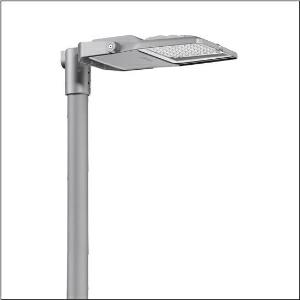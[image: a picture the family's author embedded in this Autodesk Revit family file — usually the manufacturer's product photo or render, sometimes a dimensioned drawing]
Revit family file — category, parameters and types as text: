
# Revit family: floodlight_fl_21_iq_mini___pl33t_5xa7772c4f3a_1e48
name_source: partatom
category: Lighting Fixtures
units: mm (PartAtom-declared; Revit-internal decimal feet)

## family parameters
Cut with Voids When Loaded = No
Host = Face
Light Source = No
Part Type = Normal
Room Calculation Point = No
Round Connector Dimension = Use Diameter
Shared = No

## types (1)
- --- (1 x LED, 12570 lm, 87.2 W, 4000K)
    Apparent Load = 87 VA
    CIE Flux Codes = 26 75 99 100 100
    Color Rendering = 70
    Color Temperature = 4000K
    Default Elevation = 1800 mm
    Description = Floodlight FL 21 iQ mini, floodlight, primary light control with lens, of PMMA, primary optical cover: protective disc, of toughened safety glass, transparent, light distribution: PL33T, light emission: direct distribution, installation type: surface-mounted, LED, High Power LED, rated luminous flux: 12.570lm, luminous efficacy: 144lm/W, light colour: 740, colour temperature: 4000K, control: Auto-Match, Temp-Guard, Night-Set, Smart-Wire, Desk-Remote (wireless, voltage-free reading and setting of iQ features in the workshop via application-optimized NFC function/RFID function), optimised constant luminous flux control (CLO 2.0), Light-Fading, Lumen-Switch, with terminal, 6-pole, mains connection: 220..240V, AC, 50/60Hz, start of lifetime: 87W, end of service life: 92W, reduction: 40W, luminaire housing, of diecast aluminium, powder-coated, Siteco® metallic grey (DB 702S), corrosivity category C5 mid according to DIN EN ISO 12944, sealing non-destructively replaceable, please order mast flange separately, mast bracket, of steel, galvanised, powder-coated, protection rating (complete): IP66, insulation class (complete): insulation class II (safety insulation), certification: CE, ENEC, VDE, protection symbol: D, impact resistance: IK08, permissible operating ambient temperature: -40..+40°C, permissible operating ambient temperature for outdoor applications: -40..+50°C, standard: DIN EN 12944, LABS conformity tested according to VDMA 24364:2018-05, packaging unit: 1 piece

Light Distribution: PL33T
    Height = 70 mm
    Lamp = 1 x LED
    Lamp Light Flux = 12570 lm
    Lamp Power = 87.2 W
    Lamp count = 1
    Length = 485 mm
    Luminous efficacy = 144 lm/W
    Manufacturer = Siteco
    ModVariant = No
    Model = 5XA7772C4F3A
    Number of Poles = 1
    OnlyDefault = Yes
    Power Factor = 1
    Product Name = Floodlight FL 21 iQ mini | PL33T
    Product group = floodlight | pylon annexe
    ProductGroupID = 6200
    Protection Class = Protection class II
    Protection Degree = IP 66
    RLX_Detail_Level = 1
    RLX_Emergency_Light_Flux = 0 lm
    RLX_Emergency_Type = 0
    RLX_Emergency_Type_DB = No
    RlxData = <blob elided: 101213 chars, md5=3002de67>
    Socket = socket
    Standby Power = 0 W
    System Light Flux = 12570 lm
    System Power = 87 W
    Type Comments = factory setting: luminous flux: 100 % | dim-lin: 254 | 456 mA
    Type Image = l_1007125.jpg
    URL = http://relux.com
    VarID = @adj_099505
    Voltage = 0 V
    Weight = 0.00 kg
    Width = 337 mm

## geometry (parser evidence)
native form markers: Blend x4, Sweep x14
no freeform markers — native parametric forms only
